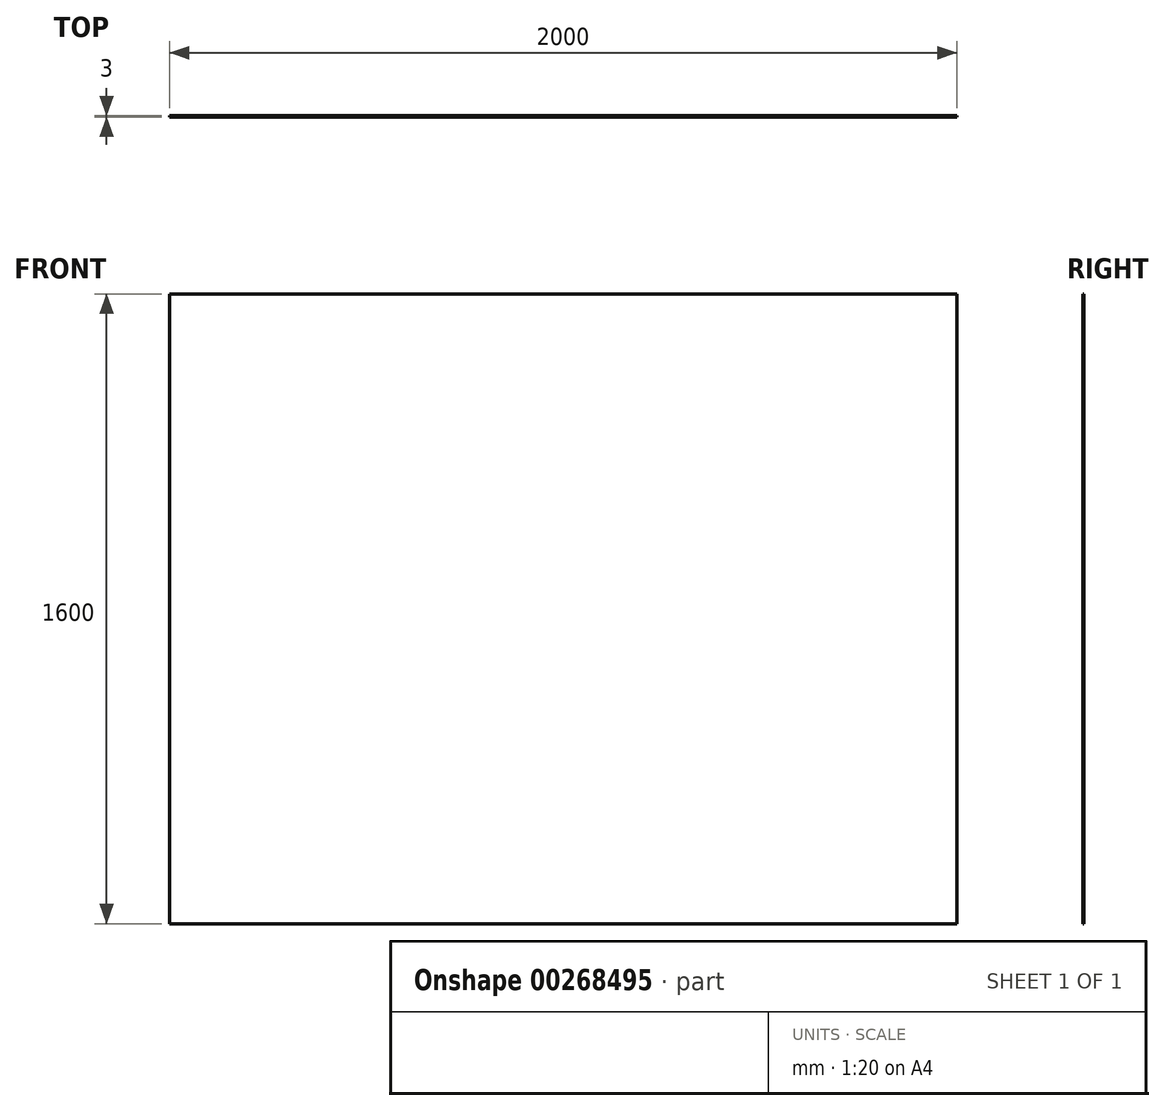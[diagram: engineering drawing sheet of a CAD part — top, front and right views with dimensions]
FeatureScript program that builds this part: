
annotation { "Feature Type Name" : "Feature", "Feature Type Description" : "" }
export const myFeature = defineFeature(function(context is Context, id is Id, definition is map)
    precondition{}
    {
        {
            var Q0;
            Q0=qCreatedBy(makeId("Front.planeOp"),FACE);
            var sketch = newSketch(context, id + "F0", { "sketchPlane" : qUnion([Q0])});
            skLineSegment(sketch, "E0.bottom", {"start": v(-996.32, 538.57) * mm, "end": v(1003.68, 538.57) * mm});
            skLineSegment(sketch, "E0.top", {"start": v(-996.32, -1061.43) * mm, "end": v(1003.68, -1061.43) * mm});
            skLineSegment(sketch, "E0.left", {"start": v(-996.32, 538.57) * mm, "end": v(-996.32, -1061.43) * mm});
            skLineSegment(sketch, "E0.right", {"start": v(1003.68, 538.57) * mm, "end": v(1003.68, -1061.43) * mm});
            skSolve(sketch);
        }
        {
            var Q0;
            Q0 = qSketchRegion(id + "F0", true);
            extrude(context, id + "F1", {"entities" : qUnion([Q0]), "depth" : 3 * mm});
        }
    });
